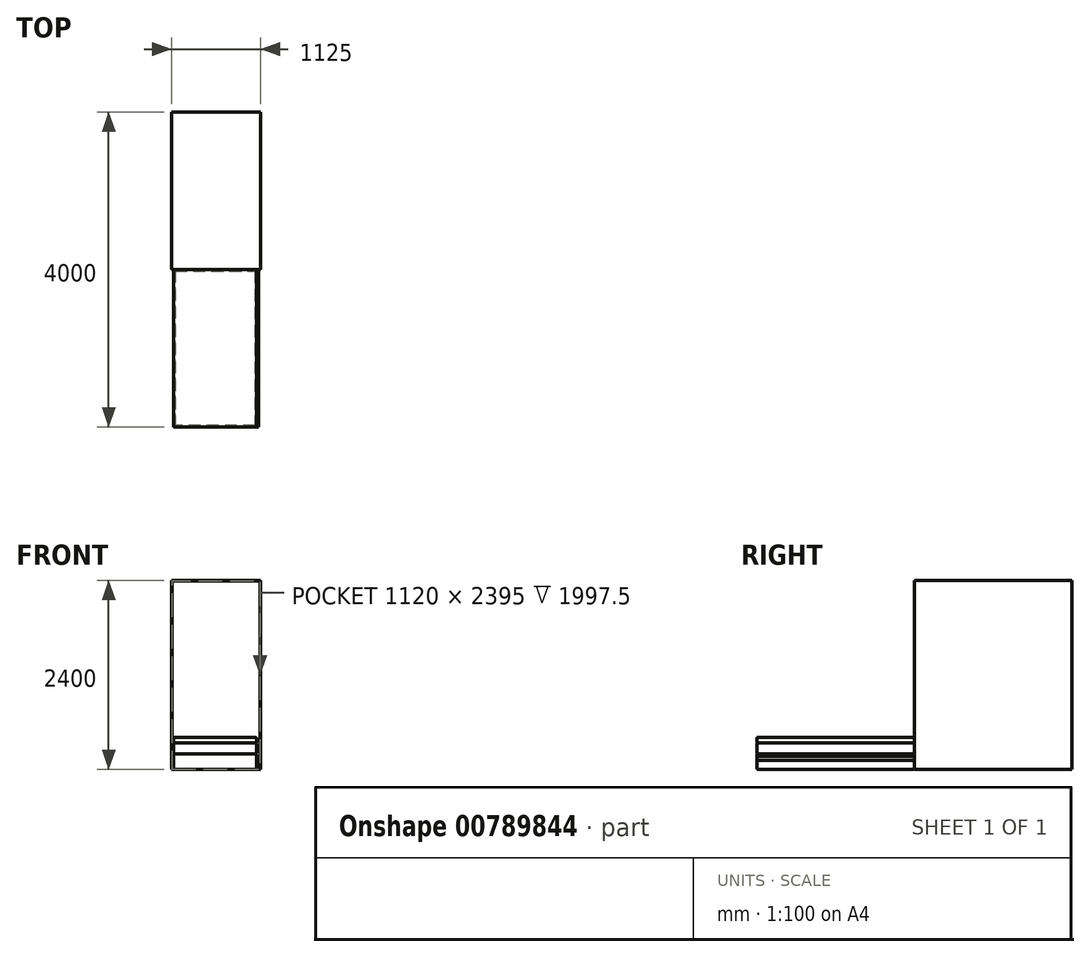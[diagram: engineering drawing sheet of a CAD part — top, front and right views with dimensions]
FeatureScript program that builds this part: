
annotation { "Feature Type Name" : "Feature", "Feature Type Description" : "" }
export const myFeature = defineFeature(function(context is Context, id is Id, definition is map)
    precondition{}
    {
        {
            var Q0;
            Q0=qCreatedBy(makeId("Top.planeOp"),FACE);
            var sketch = newSketch(context, id + "F0", { "sketchPlane" : qUnion([Q0])});
            skLineSegment(sketch, "E0", {"start": v(0, 0) * mm, "end": v(1050, 0) * mm});
            skLineSegment(sketch, "E1", {"start": v(1050, 0) * mm, "end": v(1050, -2000) * mm});
            skLineSegment(sketch, "E2", {"start": v(1050, -2000) * mm, "end": v(0, -2000) * mm});
            skLineSegment(sketch, "E3", {"start": v(0, -2000) * mm, "end": v(0, 0) * mm});
            skSolve(sketch);
        }
        {
            var Q0;
            Q0 = qSketchRegion(id + "F0", true);
            extrude(context, id + "F1", {"entities" : qUnion([Q0]), "depth" : 200 * mm, "offsetDistance" : 25 * mm});
        }
        {
            var Q0;
            Q0=makeQuery(id+"F1.opExtrude","CAP_EDGE",EDGE,{"disambiguationData":[OSD([sQuery(id+"F0.wireOp",EDGE,"E2")])],"isStart":false});
            var Q1;
            Q1=makeQuery(id+"F1.opExtrude","CAP_EDGE",EDGE,{"disambiguationData":[OSD([sQuery(id+"F0.wireOp",EDGE,"E1")])],"isStart":false});
            var Q2;
            Q2=makeQuery(id+"F1.opExtrude","CAP_EDGE",EDGE,{"disambiguationData":[OSD([sQuery(id+"F0.wireOp",EDGE,"E3")])],"isStart":false});
            var Q3;
            Q3=makeQuery(id+"F1.opExtrude","CAP_EDGE",EDGE,{"disambiguationData":[OSD([sQuery(id+"F0.wireOp",EDGE,"E0")])],"isStart":false});
            var Q4;
            Q4=makeQuery(id+"F1.opExtrude","CAP_FACE",FACE,{"disambiguationData":[OSD([sQuery(id+"F0.wireOp",EDGE,"E0"),sQuery(id+"F0.wireOp",EDGE,"E1"),sQuery(id+"F0.wireOp",EDGE,"E2"),sQuery(id+"F0.wireOp",EDGE,"E3")])],"isStart":false});
            fillet(context, id + "F2", {"entities" : qUnion([Q0, Q1, Q2, Q3, Q4]), "radius" : 20 * mm, "tangentPropagation" : true, "allowEdgeOverflow" : false});
        }
        {
            var Q0;
            Q0=makeQuery(id+"F1.opExtrude","CAP_FACE",FACE,{"disambiguationData":[OSD([sQuery(id+"F0.wireOp",EDGE,"E0"),sQuery(id+"F0.wireOp",EDGE,"E1"),sQuery(id+"F0.wireOp",EDGE,"E2"),sQuery(id+"F0.wireOp",EDGE,"E3")])],"isStart":false});
            var sketch = newSketch(context, id + "F3", { "sketchPlane" : qUnion([Q0])});
            skLineSegment(sketch, "E4.bottom", {"start": v(0, 0) * mm, "end": v(1050, 0) * mm});
            skLineSegment(sketch, "E4.top", {"start": v(0, -2000) * mm, "end": v(1050, -2000) * mm});
            skLineSegment(sketch, "E4.left", {"start": v(0, 0) * mm, "end": v(0, -2000) * mm});
            skLineSegment(sketch, "E4.right", {"start": v(1050, 0) * mm, "end": v(1050, -2000) * mm});
            skSolve(sketch);
        }
        {
            var Q0;
            Q0 = qSketchRegion(id + "F3", true);
            extrude(context, id + "F4", {"entities" : qUnion([Q0]), "operationType" : NewBodyOperationType.ADD, "depth" : 135 * mm, "offsetDistance" : 25 * mm});
        }
        {
            var Q0;
            Q0=makeQuery(id+"F4.opExtrude","CAP_EDGE",EDGE,{"disambiguationData":[OSD([sQuery(id+"F3.wireOp",EDGE,"E4.bottom")])],"isStart":true});
            var Q1;
            Q1=makeQuery(id+"F4.opExtrude","CAP_EDGE",EDGE,{"disambiguationData":[OSD([sQuery(id+"F3.wireOp",EDGE,"E4.right")])],"isStart":true});
            var Q2;
            Q2=makeQuery(id+"F4.opExtrude","CAP_EDGE",EDGE,{"disambiguationData":[OSD([sQuery(id+"F3.wireOp",EDGE,"E4.top")])],"isStart":true});
            fillet(context, id + "F5", {"entities" : qUnion([Q0, Q1, Q2]), "radius" : 15 * mm, "tangentPropagation" : true, "allowEdgeOverflow" : false});
        }
        {
            var Q0;
            Q0=makeQuery(id+"F4.opExtrude","CAP_EDGE",EDGE,{"disambiguationData":[OSD([sQuery(id+"F3.wireOp",EDGE,"E4.top")])],"isStart":false});
            var Q1;
            Q1=makeQuery(id+"F4.opExtrude","CAP_EDGE",EDGE,{"disambiguationData":[OSD([sQuery(id+"F3.wireOp",EDGE,"E4.left")])],"isStart":false});
            var Q2;
            Q2=makeQuery(id+"F4.opExtrude","CAP_EDGE",EDGE,{"disambiguationData":[OSD([sQuery(id+"F3.wireOp",EDGE,"E4.right")])],"isStart":false});
            var Q3;
            Q3=makeQuery(id+"F4.opExtrude","CAP_EDGE",EDGE,{"disambiguationData":[OSD([sQuery(id+"F3.wireOp",EDGE,"E4.bottom")])],"isStart":false});
            fillet(context, id + "F6", {"entities" : qUnion([Q0, Q1, Q2, Q3]), "radius" : 15 * mm, "tangentPropagation" : true, "allowEdgeOverflow" : false});
        }
        {
            var Q0;
            Q0=makeQuery(id+"F1.opExtrude","CAP_EDGE",EDGE,{"disambiguationData":[OSD([sQuery(id+"F0.wireOp",EDGE,"E2")])],"isStart":true});
            var Q1;
            Q1=makeQuery(id+"F1.opExtrude","CAP_EDGE",EDGE,{"disambiguationData":[OSD([sQuery(id+"F0.wireOp",EDGE,"E1")])],"isStart":true});
            var Q2;
            Q2=makeQuery(id+"F1.opExtrude","CAP_EDGE",EDGE,{"disambiguationData":[OSD([sQuery(id+"F0.wireOp",EDGE,"E3")])],"isStart":true});
            var Q3;
            Q3=makeQuery(id+"F1.opExtrude","CAP_EDGE",EDGE,{"disambiguationData":[OSD([sQuery(id+"F0.wireOp",EDGE,"E0")])],"isStart":true});
            fillet(context, id + "F7", {"entities" : qUnion([Q0, Q1, Q2, Q3]), "radius" : 20 * mm, "tangentPropagation" : true, "allowEdgeOverflow" : false});
        }
        {
            var Q0;
            Q0=makeQuery(id+"F4.opExtrude","CAP_FACE",FACE,{"disambiguationData":[OSD([sQuery(id+"F3.wireOp",EDGE,"E4.bottom"),sQuery(id+"F3.wireOp",EDGE,"E4.top"),sQuery(id+"F3.wireOp",EDGE,"E4.left"),sQuery(id+"F3.wireOp",EDGE,"E4.right")])],"isStart":false});
            var sketch = newSketch(context, id + "F8", { "sketchPlane" : qUnion([Q0])});
            skLineSegment(sketch, "E5.bottom", {"start": v(0, 0) * mm, "end": v(1050, 0) * mm});
            skLineSegment(sketch, "E5.top", {"start": v(0, -2000) * mm, "end": v(1050, -2000) * mm});
            skLineSegment(sketch, "E5.left", {"start": v(0, 0) * mm, "end": v(0, -2000) * mm});
            skLineSegment(sketch, "E5.right", {"start": v(1050, 0) * mm, "end": v(1050, -2000) * mm});
            skSolve(sketch);
        }
        {
            var Q0;
            Q0 = qSketchRegion(id + "F8", true);
            extrude(context, id + "F9", {"entities" : qUnion([Q0]), "operationType" : NewBodyOperationType.ADD, "depth" : 75 * mm, "offsetDistance" : 25 * mm});
        }
        {
            var Q0;
            Q0=makeQuery(id+"F9.opExtrude","CAP_EDGE",EDGE,{"disambiguationData":[OSD([sQuery(id+"F8.wireOp",EDGE,"E5.top")])],"isStart":true});
            var Q1;
            Q1=makeQuery(id+"F9.opExtrude","CAP_EDGE",EDGE,{"disambiguationData":[OSD([sQuery(id+"F8.wireOp",EDGE,"E5.left")])],"isStart":true});
            var Q2;
            Q2=makeQuery(id+"F9.opExtrude","CAP_EDGE",EDGE,{"disambiguationData":[OSD([sQuery(id+"F8.wireOp",EDGE,"E5.right")])],"isStart":true});
            var Q3;
            Q3=makeQuery(id+"F9.opExtrude","CAP_EDGE",EDGE,{"disambiguationData":[OSD([sQuery(id+"F8.wireOp",EDGE,"E5.bottom")])],"isStart":true});
            var Q4;
            Q4=makeQuery(id+"F9.opExtrude","CAP_EDGE",EDGE,{"disambiguationData":[OSD([sQuery(id+"F8.wireOp",EDGE,"E5.right")])],"isStart":false});
            var Q5;
            Q5=makeQuery(id+"F9.opExtrude","CAP_EDGE",EDGE,{"disambiguationData":[OSD([sQuery(id+"F8.wireOp",EDGE,"E5.bottom")])],"isStart":false});
            var Q6;
            Q6=makeQuery(id+"F9.opExtrude","CAP_EDGE",EDGE,{"disambiguationData":[OSD([sQuery(id+"F8.wireOp",EDGE,"E5.left")])],"isStart":false});
            var Q7;
            Q7=makeQuery(id+"F9.opExtrude","CAP_EDGE",EDGE,{"disambiguationData":[OSD([sQuery(id+"F8.wireOp",EDGE,"E5.top")])],"isStart":false});
            fillet(context, id + "F10", {"entities" : qUnion([Q0, Q1, Q2, Q3, Q4, Q5, Q6, Q7]), "radius" : 15 * mm, "tangentPropagation" : true, "allowEdgeOverflow" : false});
        }
        {
            var Q0;
            Q0=makeQuery(id+"F9.opExtrude","SWEPT_EDGE",EDGE,{"disambiguationData":[OSD([sQuery(id+"F8.wireOp",EDGE,"E5.top"),sQuery(id+"F8.wireOp",EDGE,"E5.right")])]});
            var Q1;
            Q1=makeQuery(id+"F4.opExtrude","SWEPT_EDGE",EDGE,{"disambiguationData":[OSD([sQuery(id+"F3.wireOp",EDGE,"E4.top"),sQuery(id+"F3.wireOp",EDGE,"E4.right")])]});
            var Q2;
            Q2=makeQuery(id+"F1.opExtrude","SWEPT_EDGE",EDGE,{"disambiguationData":[OSD([sQuery(id+"F0.wireOp",EDGE,"E1"),sQuery(id+"F0.wireOp",EDGE,"E2")])]});
            var Q3;
            Q3=makeQuery(id+"F9.opExtrude","SWEPT_EDGE",EDGE,{"disambiguationData":[OSD([sQuery(id+"F8.wireOp",EDGE,"E5.bottom"),sQuery(id+"F8.wireOp",EDGE,"E5.right")])]});
            var Q4;
            Q4=makeQuery(id+"F4.opExtrude","SWEPT_EDGE",EDGE,{"disambiguationData":[OSD([sQuery(id+"F3.wireOp",EDGE,"E4.bottom"),sQuery(id+"F3.wireOp",EDGE,"E4.right")])]});
            var Q5;
            Q5=makeQuery(id+"F1.opExtrude","SWEPT_EDGE",EDGE,{"disambiguationData":[OSD([sQuery(id+"F0.wireOp",EDGE,"E0"),sQuery(id+"F0.wireOp",EDGE,"E1")])]});
            var Q6;
            Q6=makeQuery(id+"F9.opExtrude","SWEPT_EDGE",EDGE,{"disambiguationData":[OSD([sQuery(id+"F8.wireOp",EDGE,"E5.bottom"),sQuery(id+"F8.wireOp",EDGE,"E5.left")])]});
            var Q7;
            Q7=makeQuery(id+"F4.opExtrude","SWEPT_EDGE",EDGE,{"disambiguationData":[OSD([sQuery(id+"F3.wireOp",EDGE,"E4.bottom"),sQuery(id+"F3.wireOp",EDGE,"E4.left")])]});
            var Q8;
            Q8=makeQuery(id+"F1.opExtrude","SWEPT_EDGE",EDGE,{"disambiguationData":[OSD([sQuery(id+"F0.wireOp",EDGE,"E0"),sQuery(id+"F0.wireOp",EDGE,"E3")])]});
            var Q9;
            Q9=makeQuery(id+"F9.opExtrude","SWEPT_EDGE",EDGE,{"disambiguationData":[OSD([sQuery(id+"F8.wireOp",EDGE,"E5.top"),sQuery(id+"F8.wireOp",EDGE,"E5.left")])]});
            var Q10;
            Q10=makeQuery(id+"F1.opExtrude","SWEPT_EDGE",EDGE,{"disambiguationData":[OSD([sQuery(id+"F0.wireOp",EDGE,"E2"),sQuery(id+"F0.wireOp",EDGE,"E3")])]});
            var Q11;
            Q11=makeQuery(id+"F4.opExtrude","SWEPT_EDGE",EDGE,{"disambiguationData":[OSD([sQuery(id+"F3.wireOp",EDGE,"E4.top"),sQuery(id+"F3.wireOp",EDGE,"E4.left")])]});
            fillet(context, id + "F11", {"entities" : qUnion([Q0, Q1, Q2, Q3, Q4, Q5, Q6, Q7, Q8, Q9, Q10, Q11]), "radius" : 5 * mm, "tangentPropagation" : true, "allowEdgeOverflow" : false});
        }
        {
            var Q0;
            Q0=makeQuery(id+"F1.opExtrude","SWEPT_FACE",FACE,{"disambiguationData":[OSD([sQuery(id+"F0.wireOp",EDGE,"E3")])]});
            var sketch = newSketch(context, id + "F12", { "sketchPlane" : qUnion([Q0])});
            skLineSegment(sketch, "E6", {"start": v(0, 165) * mm, "end": v(2000, 165) * mm});
            skLineSegment(sketch, "E7", {"start": v(2000, 165) * mm, "end": v(2000, 115) * mm});
            skLineSegment(sketch, "E8", {"start": v(2000, 115) * mm, "end": v(0, 115) * mm});
            skLineSegment(sketch, "E9", {"start": v(0, 115) * mm, "end": v(0, 165) * mm});
            skSolve(sketch);
        }
        {
            var Q0;
            Q0=makeQuery(id+"F1.opExtrude","SWEPT_FACE",FACE,{"disambiguationData":[OSD([sQuery(id+"F0.wireOp",EDGE,"E1")])]});
            var sketch = newSketch(context, id + "F13", { "sketchPlane" : qUnion([Q0])});
            skLineSegment(sketch, "E10", {"start": v(0, 165) * mm, "end": v(-2000, 165) * mm});
            skLineSegment(sketch, "E11", {"start": v(-2000, 165) * mm, "end": v(-2000, 115) * mm});
            skLineSegment(sketch, "E12", {"start": v(-2000, 115) * mm, "end": v(0, 115) * mm});
            skLineSegment(sketch, "E13", {"start": v(0, 115) * mm, "end": v(0, 165) * mm});
            skSolve(sketch);
        }
        {
            var Q0;
            Q0=makeQuery(id+"F13.imprint","IMPRINT",FACE,{"disambiguationData":[TD([[makeQuery(id+"F13.imprint","IMPRINT",EDGE,{"derivedFrom":sQuery(id+"F13.wireOp",EDGE,"E10")}),1.0]])]});
            extrude(context, id + "F14", {"entities" : qUnion([Q0]), "operationType" : NewBodyOperationType.ADD, "depth" : 25 * mm, "offsetDistance" : 25 * mm});
        }
        {
            var Q0;
            Q0=qCreatedBy(makeId("Top.planeOp"),FACE);
            var sketch = newSketch(context, id + "F15", { "sketchPlane" : qUnion([Q0])});
            skLineSegment(sketch, "E14", {"start": v(-25, 2000) * mm, "end": v(1100, 2000) * mm});
            skLineSegment(sketch, "E15", {"start": v(1100, 2000) * mm, "end": v(1100, 0) * mm});
            skLineSegment(sketch, "E16", {"start": v(-25, 2000) * mm, "end": v(-25, 0) * mm});
            skLineSegment(sketch, "E17", {"start": v(-25, 0) * mm, "end": v(1100, 0) * mm});
            skSolve(sketch);
        }
        {
            var Q0;
            Q0 = qSketchRegion(id + "F15", true);
            extrude(context, id + "F16", {"entities" : qUnion([Q0]), "depth" : 2400 * mm, "offsetDistance" : 25 * mm});
        }
        {
            var Q0;
            Q0=makeQuery(id+"F16.opExtrude","SWEPT_FACE",FACE,{"disambiguationData":[OSD([sQuery(id+"F15.wireOp",EDGE,"E17")])]});
            shell(context, id + "F17", {"entities" : qUnion([Q0]), "thickness" : 2.5 * mm});
        }
    });
